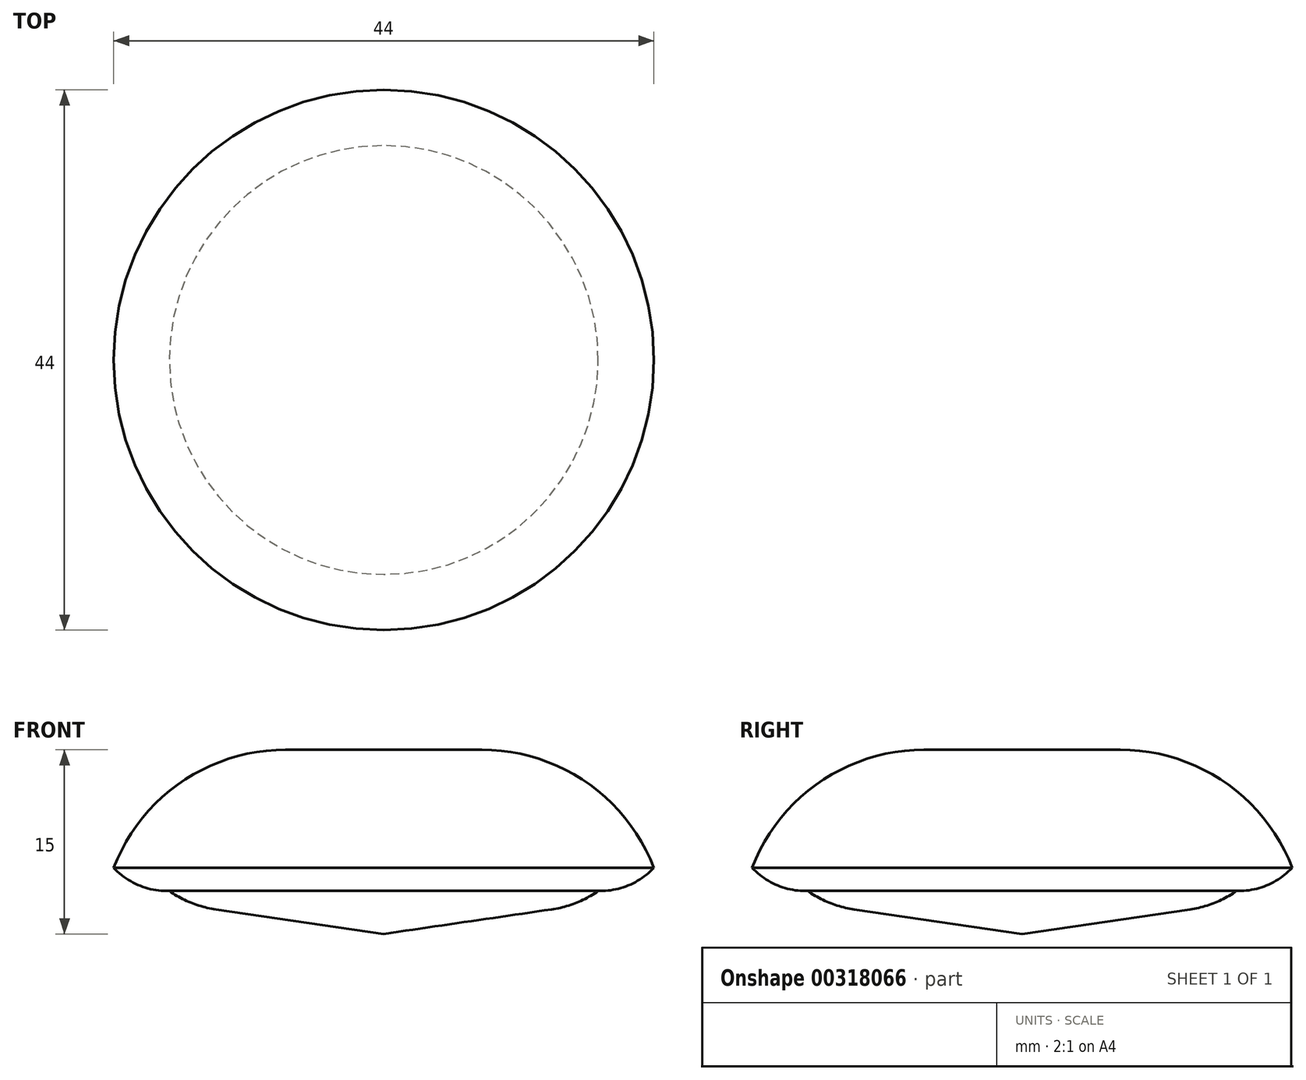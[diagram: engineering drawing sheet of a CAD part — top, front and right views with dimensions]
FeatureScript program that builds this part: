
annotation { "Feature Type Name" : "Feature", "Feature Type Description" : "" }
export const myFeature = defineFeature(function(context is Context, id is Id, definition is map)
    precondition{}
    {
        {
            var Q0;
            Q0=qCreatedBy(makeId("Front.planeOp"),FACE);
            var sketch = newSketch(context, id + "F0", { "sketchPlane" : qUnion([Q0])});
            skLineSegment(sketch, "E0", {"start": v(0, 0) * mm, "end": v(8, 0) * mm});
            skArc(sketch, "E1", {"start": v(22, -9.61) * mm, "mid": v(16.5, -2.64) * mm, "end": v(8, 0) * mm});
            skLineSegment(sketch, "E2", {"start": v(0, -15) * mm, "end": v(0, 0) * mm});
            skArc(sketch, "E3", {"start": v(17.47, -11.5) * mm, "mid": v(19.93, -11.04) * mm, "end": v(22, -9.61) * mm});
            skArc(sketch, "E4", {"start": v(13.67, -13) * mm, "mid": v(15.66, -12.48) * mm, "end": v(17.47, -11.5) * mm});
            skLineSegment(sketch, "E5", {"start": v(13.67, -13) * mm, "end": v(0, -15) * mm});
            skSolve(sketch);
        }
        {
            var Q0;
            Q0=makeQuery(id+"F0.imprint","IMPRINT",FACE,{"disambiguationData":[TD([[makeQuery(id+"F0.imprint","IMPRINT",EDGE,{"derivedFrom":sQuery(id+"F0.wireOp",EDGE,"E0")}),-1.0]])]});
            var Q1;
            Q1=sQuery(id+"F0.wireOp",EDGE,"E2");
            revolve(context, id + "F1", {"entities" : qUnion([Q0]), "axis" : qUnion([Q1]), "revolveType" : RevolveType.FULL});
        }
    });
